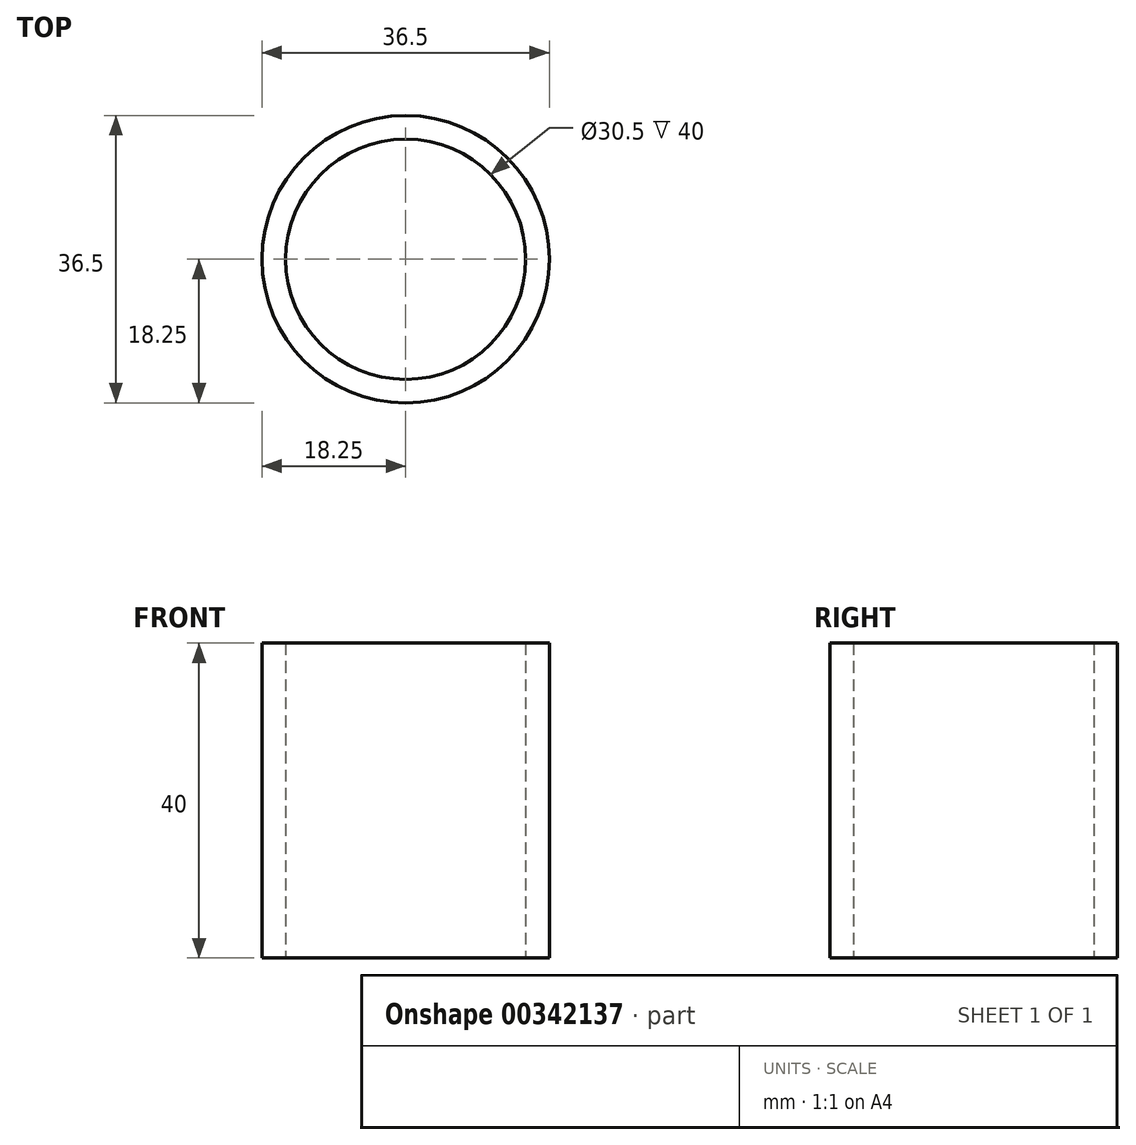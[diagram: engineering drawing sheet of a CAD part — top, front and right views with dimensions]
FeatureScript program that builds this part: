
annotation { "Feature Type Name" : "Feature", "Feature Type Description" : "" }
export const myFeature = defineFeature(function(context is Context, id is Id, definition is map)
    precondition{}
    {
        {
            var Q0;
            Q0=qCreatedBy(makeId("Top.planeOp"),FACE);
            var sketch = newSketch(context, id + "F0", { "sketchPlane" : qUnion([Q0])});
            skCircle(sketch, "E0", {"center": v(0, 0) * mm, "radius": 15.25 * mm});
            skCircle(sketch, "E1", {"center": v(0, 0) * mm, "radius": 18.25 * mm});
            skCircle(sketch, "E2", {"center": v(0, 0) * mm, "radius": 24.6 * mm, "construction": true});
            skSolve(sketch);
        }
        {
            var Q0;
            Q0=qSketchRegion(id+"F0",true);
            var Q1;
            Q1=sQuery(id+"F0.wireOp",EDGE,"E1");
            var Q2;
            Q2=sQuery(id+"F0.wireOp",EDGE,"E0");
            extrude(context, id + "F1", {"entities" : qUnion([Q0]), "surfaceEntities" : qUnion([Q1, Q2]), "endBound" : BoundingType.SYMMETRIC, "depth" : 40 * mm});
        }
    });
